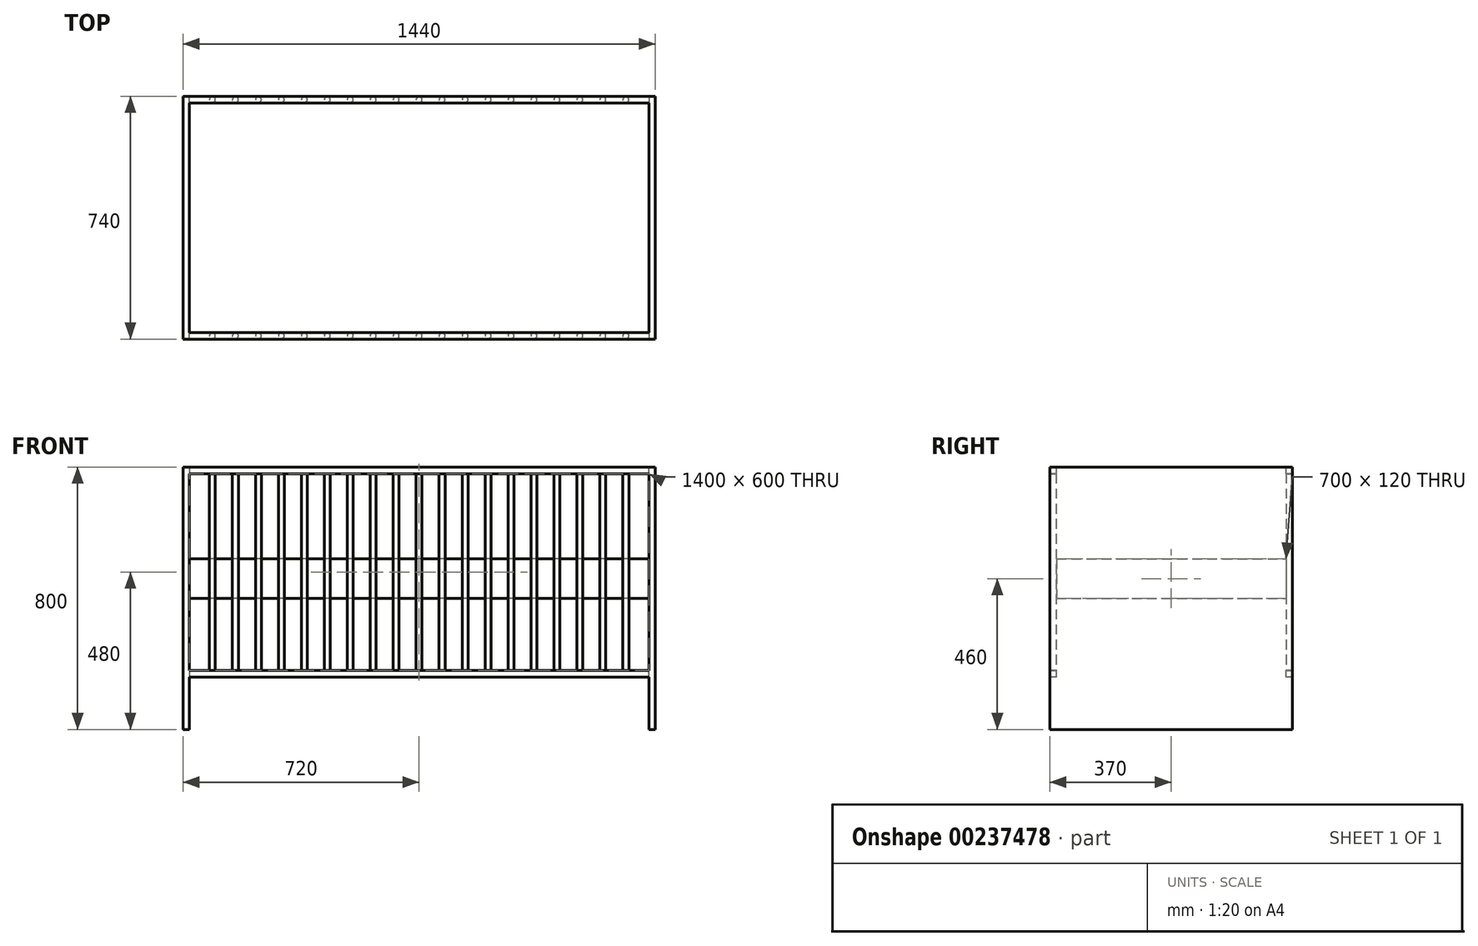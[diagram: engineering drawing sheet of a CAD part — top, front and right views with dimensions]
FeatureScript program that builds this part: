
annotation { "Feature Type Name" : "Feature", "Feature Type Description" : "" }
export const myFeature = defineFeature(function(context is Context, id is Id, definition is map)
    precondition{}
    {
        {
            var Q0;
            Q0=qCreatedBy(makeId("Top.planeOp"),FACE);
            var sketch = newSketch(context, id + "F0", { "sketchPlane" : qUnion([Q0])});
            skLineSegment(sketch, "E0.bottom", {"start": v(700, -350) * mm, "end": v(-700, -350) * mm});
            skLineSegment(sketch, "E0.top", {"start": v(700, 350) * mm, "end": v(-700, 350) * mm});
            skLineSegment(sketch, "E0.left", {"start": v(700, -350) * mm, "end": v(700, 350) * mm});
            skLineSegment(sketch, "E0.right", {"start": v(-700, -350) * mm, "end": v(-700, 350) * mm});
            skPoint(sketch, "E0.middle", {"position": v(0, 0) * mm});
            skLineSegment(sketch, "E1.0", {"start": v(-650, -300) * mm, "end": v(-650, 300) * mm});
            skLineSegment(sketch, "E1.1", {"start": v(650, -300) * mm, "end": v(-650, -300) * mm});
            skLineSegment(sketch, "E1.2", {"start": v(650, -300) * mm, "end": v(650, 300) * mm});
            skLineSegment(sketch, "E1.3", {"start": v(650, 300) * mm, "end": v(-650, 300) * mm});
            skSolve(sketch);
        }
        {
            var Q0;
            Q0=makeQuery(id+"F0.imprint","IMPRINT",FACE,{"disambiguationData":[TD([[makeQuery(id+"F0.imprint","IMPRINT",EDGE,{"derivedFrom":sQuery(id+"F0.wireOp",EDGE,"E0.bottom")}),-1.0]])]});
            extrude(context, id + "F1", {"entities" : qUnion([Q0]), "depth" : 25 * mm});
        }
        {
            var Q0;
            Q0=makeQuery(id+"F1.opExtrude","CAP_FACE",FACE,{"disambiguationData":[OSD([sQuery(id+"F0.wireOp",EDGE,"E0.bottom"),sQuery(id+"F0.wireOp",EDGE,"E0.top"),sQuery(id+"F0.wireOp",EDGE,"E0.left"),sQuery(id+"F0.wireOp",EDGE,"E0.right"),sQuery(id+"F0.wireOp",EDGE,"E1.0"),sQuery(id+"F0.wireOp",EDGE,"E1.1"),sQuery(id+"F0.wireOp",EDGE,"E1.2"),sQuery(id+"F0.wireOp",EDGE,"E1.3")])],"isStart":true});
            var sketch = newSketch(context, id + "F2", { "sketchPlane" : qUnion([Q0])});
            skLineSegment(sketch, "E2.bottom", {"start": v(-700, -370) * mm, "end": v(-720, -370) * mm});
            skLineSegment(sketch, "E2.top", {"start": v(-700, 370) * mm, "end": v(-720, 370) * mm});
            skLineSegment(sketch, "E2.left", {"start": v(-700, -370) * mm, "end": v(-700, 370) * mm});
            skLineSegment(sketch, "E2.right", {"start": v(-720, -370) * mm, "end": v(-720, 370) * mm});
            skPoint(sketch, "E2.middle", {"position": v(-710, 0) * mm});
            skLineSegment(sketch, "E3", {"start": v(0, 0) * mm, "end": v(0, 202.76) * mm, "construction": true});
            skLineSegment(sketch, "E4.MirrorCS", {"start": v(700, 370) * mm, "end": v(720, 370) * mm});
            skLineSegment(sketch, "E5.MirrorCS", {"start": v(700, -370) * mm, "end": v(720, -370) * mm});
            skLineSegment(sketch, "E6.MirrorCS", {"start": v(700, -370) * mm, "end": v(700, 370) * mm});
            skLineSegment(sketch, "E7.MirrorCS", {"start": v(720, -370) * mm, "end": v(720, 370) * mm});
            skPoint(sketch, "E8.MirrorP", {"position": v(710, 0) * mm});
            skSolve(sketch);
        }
        {
            var Q0;
            {var subQ3=sQuery(id+"F2.wireOp",EDGE,"E2.bottom");Q0=makeQuery(id+"F2.imprint","IMPRINT",FACE,{"disambiguationData":[TD([[makeQuery(id+"F2.imprint","IMPRINT",EDGE,{"derivedFrom":subQ3}),-1.0]])]});}
            var Q1;
            {var subQ4=sQuery(id+"F2.wireOp",EDGE,"E4.MirrorCS");Q1=makeQuery(id+"F2.imprint","IMPRINT",FACE,{"disambiguationData":[TD([[makeQuery(id+"F2.imprint","IMPRINT",EDGE,{"derivedFrom":subQ4}),-1.0]])]});}
            extrude(context, id + "F3", {"entities" : qUnion([Q0, Q1]), "operationType" : NewBodyOperationType.ADD, "depth" : 400 * mm, "hasSecondDirection" : true, "secondDirectionOppositeDirection" : true, "secondDirectionDepth" : 400 * mm});
        }
        {
            var Q0;
            Q0=makeQuery(id+"F3.opExtrude","SWEPT_FACE",FACE,{"disambiguationData":[OSD([sQuery(id+"F2.wireOp",EDGE,"E2.left")])]});
            var sketch = newSketch(context, id + "F4", { "sketchPlane" : qUnion([Q0])});
            skLineSegment(sketch, "E9.bottom", {"start": v(-370, 400) * mm, "end": v(-350, 400) * mm});
            skLineSegment(sketch, "E9.top", {"start": v(-370, 380) * mm, "end": v(-350, 380) * mm});
            skLineSegment(sketch, "E9.left", {"start": v(-370, 400) * mm, "end": v(-370, 380) * mm});
            skLineSegment(sketch, "E9.right", {"start": v(-350, 400) * mm, "end": v(-350, 380) * mm});
            skLineSegment(sketch, "E10.bottom", {"start": v(350, 400) * mm, "end": v(370, 400) * mm});
            skLineSegment(sketch, "E10.top", {"start": v(350, 380) * mm, "end": v(370, 380) * mm});
            skLineSegment(sketch, "E10.left", {"start": v(350, 400) * mm, "end": v(350, 380) * mm});
            skLineSegment(sketch, "E10.right", {"start": v(370, 400) * mm, "end": v(370, 380) * mm});
            skLineSegment(sketch, "E11.bottom", {"start": v(-370, -220) * mm, "end": v(-350, -220) * mm});
            skLineSegment(sketch, "E11.top", {"start": v(-370, -240) * mm, "end": v(-350, -240) * mm});
            skLineSegment(sketch, "E11.left", {"start": v(-370, -220) * mm, "end": v(-370, -240) * mm});
            skLineSegment(sketch, "E11.right", {"start": v(-350, -220) * mm, "end": v(-350, -240) * mm});
            skPoint(sketch, "E12.firstSnap0", {"position": v(-360, -220) * mm});
            skLineSegment(sketch, "E12.bottom", {"start": v(350, -220) * mm, "end": v(370, -220) * mm});
            skLineSegment(sketch, "E12.top", {"start": v(350, -240) * mm, "end": v(370, -240) * mm});
            skLineSegment(sketch, "E12.left", {"start": v(350, -220) * mm, "end": v(350, -240) * mm});
            skLineSegment(sketch, "E12.right", {"start": v(370, -220) * mm, "end": v(370, -240) * mm});
            skSolve(sketch);
        }
        {
            var Q0;
            Q0=qSketchRegion(id+"F4",true);
            var Q1;
            Q1=makeQuery(id+"F3.opExtrude","SWEPT_FACE",FACE,{"disambiguationData":[OSD([sQuery(id+"F2.wireOp",EDGE,"E6.MirrorCS")])]});
            extrude(context, id + "F5", {"entities" : qUnion([Q0]), "operationType" : NewBodyOperationType.ADD, "endBound" : BoundingType.UP_TO_SURFACE, "endBoundEntityFace" : qUnion([Q1]), "depth" : 25 * mm});
        }
        {
            var Q0;
            Q0=makeQuery(id+"F5.opExtrude","SWEPT_FACE",FACE,{"disambiguationData":[OSD([sQuery(id+"F4.wireOp",EDGE,"E11.bottom")])]});
            var sketch = newSketch(context, id + "F6", { "sketchPlane" : qUnion([Q0])});
            skCircle(sketch, "E13", {"center": v(630, -360) * mm, "radius": 9 * mm});
            skCircle(sketch, "E14.1.0.0", {"center": v(560, -360) * mm, "radius": 9 * mm});
            skCircle(sketch, "E14.2.0.0", {"center": v(490, -360) * mm, "radius": 9 * mm});
            skLineSegment(sketch, "E14.direction1", {"start": v(630, -360) * mm, "end": v(560, -360) * mm, "construction": true});
            skCircle(sketch, "E15.0.3.0", {"center": v(420, -360) * mm, "radius": 9 * mm});
            skCircle(sketch, "E15.0.4.0", {"center": v(350, -360) * mm, "radius": 9 * mm});
            skCircle(sketch, "E15.0.5.0", {"center": v(280, -360) * mm, "radius": 9 * mm});
            skCircle(sketch, "E15.0.6.0", {"center": v(210, -360) * mm, "radius": 9 * mm});
            skCircle(sketch, "E15.0.7.0", {"center": v(140, -360) * mm, "radius": 9 * mm});
            skCircle(sketch, "E15.0.8.0", {"center": v(70, -360) * mm, "radius": 9 * mm});
            skCircle(sketch, "E15.0.9.0", {"center": v(0, -360) * mm, "radius": 9 * mm});
            skCircle(sketch, "E15.0.10.0", {"center": v(-70, -360) * mm, "radius": 9 * mm});
            skCircle(sketch, "E15.0.11.0", {"center": v(-140, -360) * mm, "radius": 9 * mm});
            skCircle(sketch, "E15.0.12.0", {"center": v(-210, -360) * mm, "radius": 9 * mm});
            skCircle(sketch, "E15.0.13.0", {"center": v(-280, -360) * mm, "radius": 9 * mm});
            skCircle(sketch, "E15.0.14.0", {"center": v(-350, -360) * mm, "radius": 9 * mm});
            skCircle(sketch, "E15.0.15.0", {"center": v(-420, -360) * mm, "radius": 9 * mm});
            skCircle(sketch, "E15.0.16.0", {"center": v(-490, -360) * mm, "radius": 9 * mm});
            skCircle(sketch, "E15.0.17.0", {"center": v(-560, -360) * mm, "radius": 9 * mm});
            skCircle(sketch, "E15.0.18.0", {"center": v(-630, -360) * mm, "radius": 9 * mm});
            skCircle(sketch, "E16.MirrorC", {"center": v(630, 360) * mm, "radius": 9 * mm});
            skCircle(sketch, "E17.MirrorC", {"center": v(560, 360) * mm, "radius": 9 * mm});
            skCircle(sketch, "E18.MirrorC", {"center": v(140, 360) * mm, "radius": 9 * mm});
            skCircle(sketch, "E19.MirrorC", {"center": v(70, 360) * mm, "radius": 9 * mm});
            skCircle(sketch, "E20.MirrorC", {"center": v(-420, 360) * mm, "radius": 9 * mm});
            skCircle(sketch, "E21.MirrorC", {"center": v(0, 360) * mm, "radius": 9 * mm});
            skCircle(sketch, "E22.MirrorC", {"center": v(-70, 360) * mm, "radius": 9 * mm});
            skCircle(sketch, "E23.MirrorC", {"center": v(-140, 360) * mm, "radius": 9 * mm});
            skCircle(sketch, "E24.MirrorC", {"center": v(-210, 360) * mm, "radius": 9 * mm});
            skCircle(sketch, "E25.MirrorC", {"center": v(-280, 360) * mm, "radius": 9 * mm});
            skCircle(sketch, "E26.MirrorC", {"center": v(-490, 360) * mm, "radius": 9 * mm});
            skCircle(sketch, "E27.MirrorC", {"center": v(-560, 360) * mm, "radius": 9 * mm});
            skCircle(sketch, "E28.MirrorC", {"center": v(-630, 360) * mm, "radius": 9 * mm});
            skCircle(sketch, "E29.MirrorC", {"center": v(-350, 360) * mm, "radius": 9 * mm});
            skCircle(sketch, "E30.MirrorC", {"center": v(490, 360) * mm, "radius": 9 * mm});
            skCircle(sketch, "E31.MirrorC", {"center": v(420, 360) * mm, "radius": 9 * mm});
            skCircle(sketch, "E32.MirrorC", {"center": v(350, 360) * mm, "radius": 9 * mm});
            skCircle(sketch, "E33.MirrorC", {"center": v(280, 360) * mm, "radius": 9 * mm});
            skCircle(sketch, "E34.MirrorC", {"center": v(210, 360) * mm, "radius": 9 * mm});
            skSolve(sketch);
        }
        {
            var Q0;
            Q0=qSketchRegion(id+"F6",true);
            var Q1;
            Q1=makeQuery(id+"F5.opExtrude","SWEPT_FACE",FACE,{"disambiguationData":[OSD([sQuery(id+"F4.wireOp",EDGE,"E10.top")])]});
            extrude(context, id + "F7", {"entities" : qUnion([Q0]), "operationType" : NewBodyOperationType.ADD, "endBound" : BoundingType.UP_TO_SURFACE, "endBoundEntityFace" : qUnion([Q1]), "depth" : 300 * mm});
        }
        {
            var Q0;
            Q0=makeQuery(id+"F0.imprint","IMPRINT",FACE,{"disambiguationData":[TD([[makeQuery(id+"F0.imprint","IMPRINT",EDGE,{"derivedFrom":sQuery(id+"F0.wireOp",EDGE,"E1.0")}),-1.0]])]});
            extrude(context, id + "F8", {"entities" : qUnion([Q0]), "depth" : 120 * mm});
        }
        {
            var Q0;
            Q0=makeQuery(id+"F1.opExtrude","CAP_FACE",FACE,{"disambiguationData":[OSD([sQuery(id+"F0.wireOp",EDGE,"E0.bottom"),sQuery(id+"F0.wireOp",EDGE,"E0.top"),sQuery(id+"F0.wireOp",EDGE,"E0.left"),sQuery(id+"F0.wireOp",EDGE,"E0.right"),sQuery(id+"F0.wireOp",EDGE,"E1.0"),sQuery(id+"F0.wireOp",EDGE,"E1.1"),sQuery(id+"F0.wireOp",EDGE,"E1.2"),sQuery(id+"F0.wireOp",EDGE,"E1.3")])],"isStart":false});
            var Q1;
            Q1=makeQuery(id+"F8.opExtrude","CAP_FACE",FACE,{"disambiguationData":[OSD([sQuery(id+"F0.wireOp",EDGE,"E1.0"),sQuery(id+"F0.wireOp",EDGE,"E1.1"),sQuery(id+"F0.wireOp",EDGE,"E1.2"),sQuery(id+"F0.wireOp",EDGE,"E1.3")])],"isStart":false});
            extrude(context, id + "F9", {"entities" : qUnion([Q0]), "operationType" : NewBodyOperationType.ADD, "endBound" : BoundingType.UP_TO_SURFACE, "endBoundEntityFace" : qUnion([Q1]), "depth" : 25 * mm});
        }
    });
